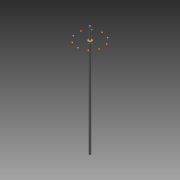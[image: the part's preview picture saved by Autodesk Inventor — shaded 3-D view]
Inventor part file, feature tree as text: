
AUTODESK INVENTOR PART (.ipt)
format: ipt  version: 2011 (Build 150239000, 239)  size: 322,560 bytes
history: native  units: mm (DEFAULTED — no unit token found)
features: other x8, sketch x4, plane x3, extrude x2, pattern_circular x1
ambient origin geometry x5: Origin, X Axis, Y Axis, Z Axis, Center Point
bodies: Solid1 (feature_tree)
feature tree (18):
  other  "Tooth Plane"
  other  "Base Body Sketch"
  other  "Base Body"
  other  "Base Body2"
  plane  "Work Plane13"
  other  "Tooth"
  pattern_circular  "Tooth Pattern"  [2 undecoded]
  plane  "Work Plane14"
  plane  "Work Plane15"
  extrude  "Extrusion2"  Depth=1.677788mm
  sketch  "Sketch11"  dims[d38=3.355575mm]
  sketch  "Sketch12"  dims[d39=3.490659mm d40=1.275119mm d41=1.677788mm d42=0.316256mm d43=90.0deg d44=100.0mm d46=360.0deg d50=7.019286mm d68=3.355575mm d69=0.0mm d73=0.0mm d75=3.141593mm d77=3.355575mm d78=2.6mm d79=0.0mm d80=0.0mm d81=0.0mm d82=0.0mm d83=3.141593mm d84=0.0mm d85=180.0deg d86=3.355575mm d87=4.362248mm d89=2.68446mm d90=90.0deg d92=2.6mm d93=3.355575mm d97=2.0mm d98=101.804mm d99=0.0mm d100=12.938mm d101=0.0mm]
  extrude  "Extrusion3"  Depth=0.316256mm
  other  "Tooth Sketch"
  sketch  "Sketch8"  dims[d35=90.0deg]
  other  "Srf1"
  sketch  "Sketch10"  dims[d37=-0.996687mm]
  other  "Pitch Diameter"
note: 2 required parameter values undecoded (feature->parameter linkage not recoverable at this tier; creation-order binding heuristic only, values carry confidence <= 0.55)
